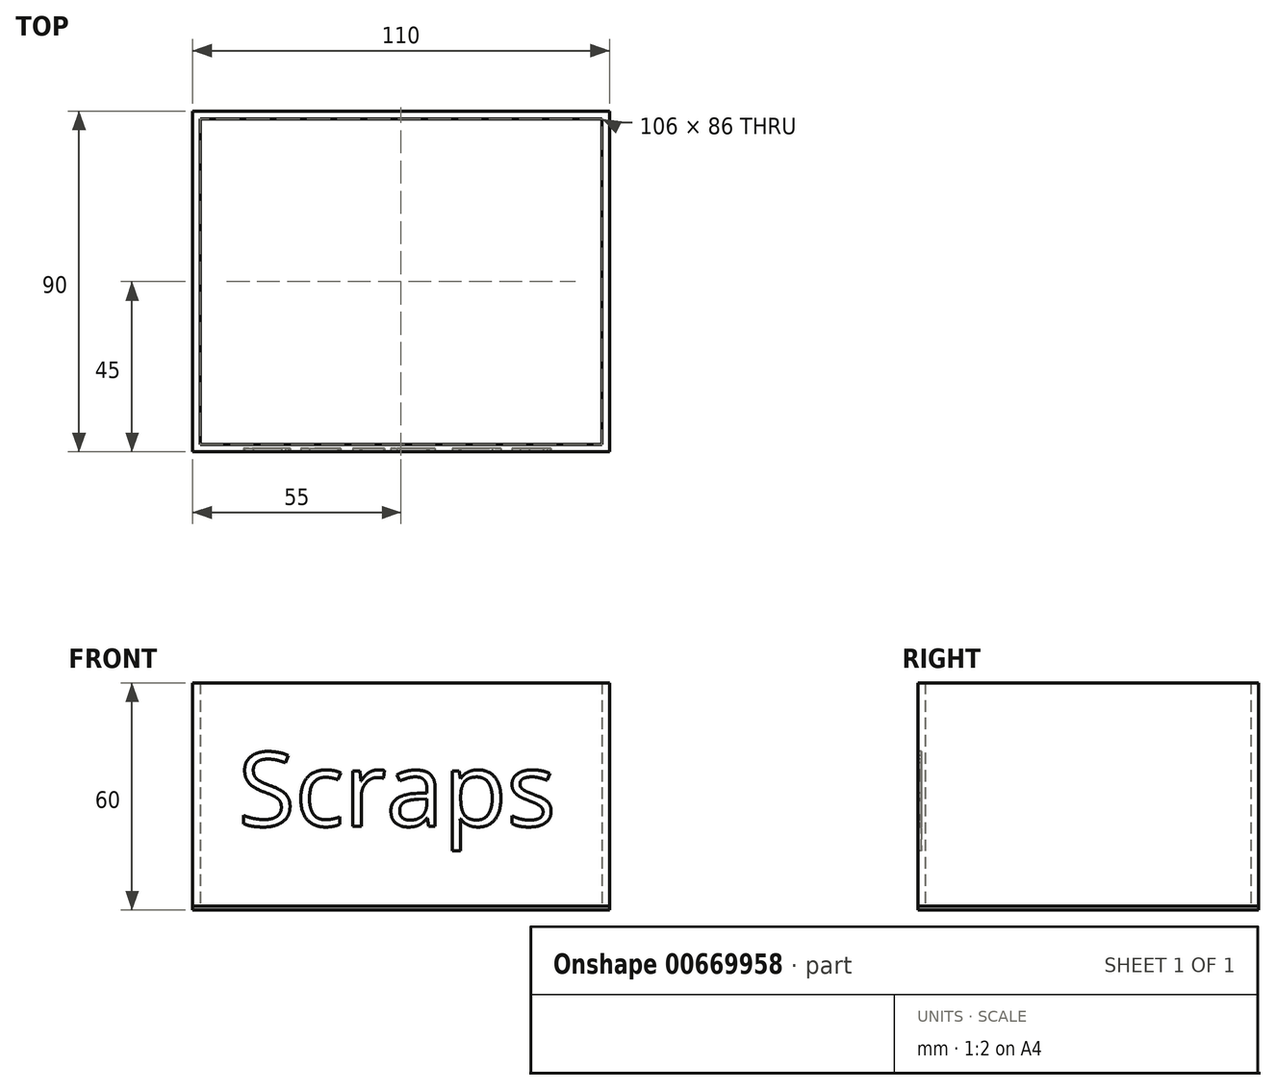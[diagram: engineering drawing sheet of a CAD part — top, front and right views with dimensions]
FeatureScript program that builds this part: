
annotation { "Feature Type Name" : "Feature", "Feature Type Description" : "" }
export const myFeature = defineFeature(function(context is Context, id is Id, definition is map)
    precondition{}
    {
        {
            var Q0;
            Q0=qCreatedBy(makeId("Top.planeOp"),FACE);
            var sketch = newSketch(context, id + "F0", { "sketchPlane" : qUnion([Q0])});
            skLineSegment(sketch, "E0.bottom", {"start": v(-55, 45) * mm, "end": v(55, 45) * mm});
            skLineSegment(sketch, "E0.top", {"start": v(-55, -45) * mm, "end": v(55, -45) * mm});
            skLineSegment(sketch, "E0.left", {"start": v(-55, 45) * mm, "end": v(-55, -45) * mm});
            skLineSegment(sketch, "E0.right", {"start": v(55, 45) * mm, "end": v(55, -45) * mm});
            skPoint(sketch, "E1", {"position": v(55, 0) * mm});
            skPoint(sketch, "E2", {"position": v(0, -45) * mm});
            skLineSegment(sketch, "E3.0", {"start": v(-53, 43) * mm, "end": v(53, 43) * mm});
            skLineSegment(sketch, "E3.1", {"start": v(-53, 43) * mm, "end": v(-53, -43) * mm});
            skLineSegment(sketch, "E3.2", {"start": v(-53, -43) * mm, "end": v(53, -43) * mm});
            skLineSegment(sketch, "E3.3", {"start": v(53, 43) * mm, "end": v(53, -43) * mm});
            skSolve(sketch);
        }
        {
            var Q0;
            Q0 = qSketchRegion(id + "F0", true);
            var Q1;
            Q1=makeQuery(id+"F0.imprint","IMPRINT",FACE,{"disambiguationData":[TD([[makeQuery(id+"F0.imprint","IMPRINT",EDGE,{"derivedFrom":sQuery(id+"F0.wireOp",EDGE,"E3.0")}),-1.0]])]});
            extrude(context, id + "F1", {"entities" : qUnion([Q0, Q1]), "depth" : 1 * mm, "offsetDistance" : 25 * mm});
        }
        {
            var Q0;
            Q0=makeQuery(id+"F0.imprint","IMPRINT",FACE,{"disambiguationData":[TD([[makeQuery(id+"F0.imprint","IMPRINT",EDGE,{"derivedFrom":sQuery(id+"F0.wireOp",EDGE,"E0.bottom")}),-1.0]])]});
            extrude(context, id + "F2", {"entities" : qUnion([Q0]), "depth" : 60 * mm, "offsetDistance" : 25 * mm});
        }
        {
            var Q0;
            Q0=makeQuery(id+"F2.opExtrude","SWEPT_FACE",FACE,{"disambiguationData":[OSD([sQuery(id+"F0.wireOp",EDGE,"E0.top")])]});
            var sketch = newSketch(context, id + "F3", { "sketchPlane" : qUnion([Q0])});
            skText(sketch, "E4", { "text": "Scraps", "fontName": "OpenSans-Regular.ttf"});
            const initialGuessF3  = {"E4": [-0.04296, 0.02219, 1, 0, 0.0196]};
            skSetInitialGuess(sketch, initialGuessF3);
            skSolve(sketch);
        }
        {
            var Q0;
            Q0 = qSketchRegion(id + "F3", true);
            extrude(context, id + "F4", {"entities" : qUnion([Q0]), "operationType" : NewBodyOperationType.REMOVE, "oppositeDirection" : true, "depth" : 1 * mm, "offsetDistance" : 25 * mm});
        }
    });
